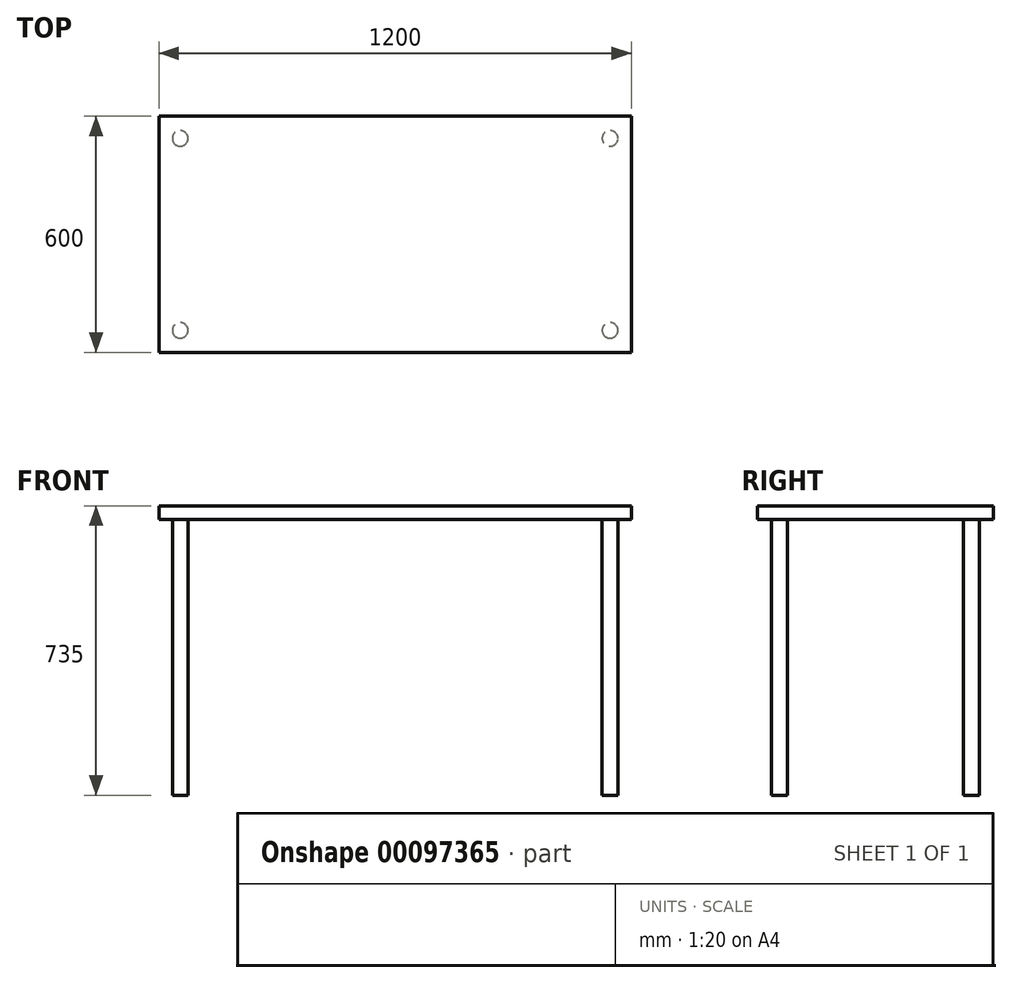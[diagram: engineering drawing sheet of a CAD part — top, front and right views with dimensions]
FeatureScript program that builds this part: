
annotation { "Feature Type Name" : "Feature", "Feature Type Description" : "" }
export const myFeature = defineFeature(function(context is Context, id is Id, definition is map)
    precondition{}
    {
        {
            var Q0;
            Q0=qCreatedBy(makeId("Top.planeOp"),FACE);
            var sketch = newSketch(context, id + "F0", { "sketchPlane" : qUnion([Q0])});
            skLineSegment(sketch, "E0.bottom", {"start": v(600, 300) * mm, "end": v(-600, 300) * mm});
            skLineSegment(sketch, "E0.top", {"start": v(600, -300) * mm, "end": v(-600, -300) * mm});
            skLineSegment(sketch, "E0.left", {"start": v(600, 300) * mm, "end": v(600, -300) * mm});
            skLineSegment(sketch, "E0.right", {"start": v(-600, 300) * mm, "end": v(-600, -300) * mm});
            skPoint(sketch, "E0.middle", {"position": v(0, 0) * mm});
            skSolve(sketch);
        }
        {
            var Q0;
            Q0=makeQuery(id+"F0.imprint","IMPRINT",FACE,{"disambiguationData":[TD([[makeQuery(id+"F0.imprint","IMPRINT",EDGE,{"derivedFrom":sQuery(id+"F0.wireOp",EDGE,"E0.bottom")}),1.0]])]});
            extrude(context, id + "F1", {"entities" : qUnion([Q0]), "depth" : 35 * mm});
        }
        {
            var Q0;
            Q0=makeQuery(id+"F1.opExtrude","CAP_FACE",FACE,{"disambiguationData":[OSD([sQuery(id+"F0.wireOp",EDGE,"E0.bottom"),sQuery(id+"F0.wireOp",EDGE,"E0.top"),sQuery(id+"F0.wireOp",EDGE,"E0.left"),sQuery(id+"F0.wireOp",EDGE,"E0.right")])],"isStart":true});
            var sketch = newSketch(context, id + "F2", { "sketchPlane" : qUnion([Q0])});
            skCircle(sketch, "E1", {"center": v(545.98, -243.87) * mm, "radius": 20 * mm});
            skCircle(sketch, "E2", {"center": v(545.98, 243.87) * mm, "radius": 20 * mm});
            skCircle(sketch, "E3", {"center": v(-545.98, 243.87) * mm, "radius": 20 * mm});
            skCircle(sketch, "E4", {"center": v(-545.98, -243.87) * mm, "radius": 20 * mm});
            skLineSegment(sketch, "E5", {"start": v(0, -300) * mm, "end": v(0, 300) * mm, "construction": true});
            skLineSegment(sketch, "E6", {"start": v(-600, 0) * mm, "end": v(600, 0) * mm, "construction": true});
            skSolve(sketch);
        }
        {
            var Q0;
            Q0=makeQuery(id+"F2.imprint","IMPRINT",FACE,{"disambiguationData":[TD([[makeQuery(id+"F2.imprint","IMPRINT",EDGE,{"derivedFrom":sQuery(id+"F2.wireOp",EDGE,"E3")}),1.0]])]});
            var Q1;
            Q1=makeQuery(id+"F2.imprint","IMPRINT",FACE,{"disambiguationData":[TD([[makeQuery(id+"F2.imprint","IMPRINT",EDGE,{"derivedFrom":sQuery(id+"F2.wireOp",EDGE,"E4")}),1.0]])]});
            var Q2;
            Q2=makeQuery(id+"F2.imprint","IMPRINT",FACE,{"disambiguationData":[TD([[makeQuery(id+"F2.imprint","IMPRINT",EDGE,{"derivedFrom":sQuery(id+"F2.wireOp",EDGE,"E2")}),1.0]])]});
            var Q3;
            Q3=makeQuery(id+"F2.imprint","IMPRINT",FACE,{"disambiguationData":[TD([[makeQuery(id+"F2.imprint","IMPRINT",EDGE,{"derivedFrom":sQuery(id+"F2.wireOp",EDGE,"E1")}),1.0]])]});
            extrude(context, id + "F3", {"entities" : qUnion([Q0, Q1, Q2, Q3]), "operationType" : NewBodyOperationType.ADD, "depth" : 700 * mm});
        }
    });
